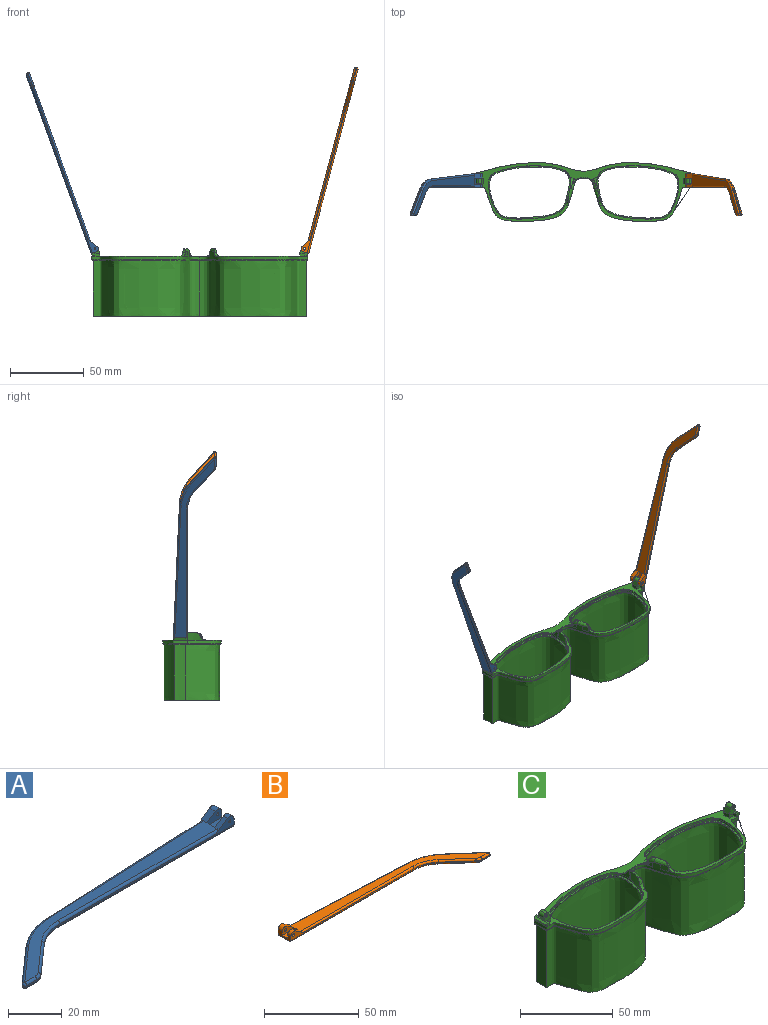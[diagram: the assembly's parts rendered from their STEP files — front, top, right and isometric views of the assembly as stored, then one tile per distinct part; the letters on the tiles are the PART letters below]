
ASSEMBLY  parts=3 mates=2
PART A: 43 faces, bbox 130.2x29.5x5.9 mm
  f0: plane 9.62x3.72mm, normal (1,0,0), area 24.7mm2, adj f1,f3,f4,f5,f10,f16,f18,f28
  f1: cylinder r=2.2mm len=3.45mm, axis (0,-1,0), area 11mm2, adj f0,f2,f4,f37
  f2: plane 6.01x3.91mm, normal (-0.55,0,0.84), area 12.7mm2, adj f1,f4,f9,f19,f37
  f3: plane 2.26x0.1mm, normal (0,0,1), area 0.1mm2, adj f0,f5,f18
  f4: plane 92.1x4.9mm, normal (0,-1,0), area 79.9mm2, adj f0,f1,f2,f14,f19,f36,f42
  f5: plane 93.42x4.13mm, normal (-0.04,1,0), area 64.8mm2, adj f0,f3,f11,f15,f17,f27,f28
  f6: plane 17.82x15.72mm, normal (-0.66,0.75,0), area 14.3mm2, adj f11,f12,f25,f30
  f7: plane 5.46x0.6mm, normal (0,-1,0), area 3.3mm2, adj f12,f13,f23,f32
  f8: plane 14.99x13.23mm, normal (0.66,-0.75,0), area 12mm2, adj f13,f14,f21,f34
  f9: plane 121.18x26.73mm, normal (0,0,1), area 627.7mm2, adj f2,f17,f19,f20,f21,f22,f23,f25
  f10: plane 129.1x27.08mm, normal (0,0,-1), area 686.5mm2, adj f0,f28,f29,f30,f32,f33,f34,f35
  f11: cylinder r=30mm len=18.52mm, axis (0,0,-1), area 12.2mm2, adj f5,f6,f26,f29
  f12: cylinder r=1mm len=1.75mm, axis (0,0,-1), area 1.5mm2, adj f6,f7,f24,f31
  f13: cylinder r=5mm len=3.31mm, axis (0,0,-1), area 2.2mm2, adj f7,f8,f22,f33
  f14: cylinder r=20mm len=13.23mm, axis (0,0,1), area 8.7mm2, adj f4,f8,f20,f35
  f15: plane 5.66x0.25mm, normal (0,0,-1), area 0.7mm2, adj f5,f17,f18
  f16: cylinder r=2.2mm len=3.45mm, axis (0,-1,0), area 14.8mm2, adj f0,f17,f18,f38
  f17: plane 6.01x3.91mm, normal (-0.55,0,0.84), area 16.9mm2, adj f5,f9,f15,f16,f18,f27,f38
  f18: plane 7.92x3.3mm, normal (0,1,0), area 15.9mm2, adj f0,f3,f15,f16,f17,f41
  f19: cylinder r=1mm len=84.18mm, axis (-1,0,0), area 131.4mm2, adj f2,f4,f9,f20
  f20: torus R=21mm, axis (0,0,1), area 23.1mm2, adj f9,f14,f19,f21
  f21: cylinder r=1mm len=15.65mm, axis (-0.75,-0.66,0), area 31.4mm2, adj f8,f9,f20,f22
  f22: torus R=4mm, axis (0,0,1), area 5.3mm2, adj f9,f13,f21,f23
  f23: cylinder r=1mm len=5.46mm, axis (-1,0,0), area 8.6mm2, adj f7,f9,f22,f24
  f24: sphere r=1mm, area 2.4mm2, adj f12,f23,f25
  f25: cylinder r=1mm len=18.48mm, axis (0.75,0.66,0), area 37.3mm2, adj f6,f9,f24,f26
  f26: torus R=29mm, axis (0,0,1), area 31.6mm2, adj f9,f11,f25,f27
  f27: cylinder r=1mm len=85.5mm, axis (1,0.04,0), area 133.5mm2, adj f5,f9,f17,f26
  f28: cylinder r=1mm len=93.46mm, axis (-1,-0.04,0), area 146.9mm2, adj f0,f5,f10,f29
  f29: torus R=29mm, axis (0,0,1), area 31.6mm2, adj f10,f11,f28,f30
  f30: cylinder r=1mm len=18.48mm, axis (-0.75,-0.66,0), area 37.3mm2, adj f6,f10,f29,f31
  f31: sphere r=1mm, area 2.4mm2, adj f12,f30,f32
  f32: cylinder r=1mm len=5.46mm, axis (1,0,0), area 8.6mm2, adj f7,f10,f31,f33
  f33: torus R=4mm, axis (0,0,1), area 5.3mm2, adj f10,f13,f32,f34
  f34: cylinder r=1mm len=15.65mm, axis (0.75,0.66,0), area 31.4mm2, adj f8,f10,f33,f35
  f35: torus R=21mm, axis (0,0,1), area 23.1mm2, adj f10,f14,f34,f36
  f36: cylinder r=1mm len=92.1mm, axis (1,0,0), area 144.7mm2, adj f0,f4,f10,f35
  f37: plane 7.92x4.7mm, normal (0,1,0), area 27mm2, adj f0,f1,f2,f39,f40,f42
  f38: plane 7.92x4.7mm, normal (0,-1,0), area 27mm2, adj f0,f16,f17,f39,f40,f41
  f39: plane 7.92x4.1mm, normal (0,0,1), area 32.5mm2, adj f0,f37,f38,f40
  f40: plane 4.1x1.4mm, normal (1,0,0), area 5.7mm2, adj f9,f37,f38,f39
  f41: cylinder r=0.5mm len=3.1mm, axis (0,-1,0), area 9.7mm2, adj f18,f38
  f42: cylinder r=0.5mm len=2.3mm, axis (0,-1,0), area 7.2mm2, adj f4,f37
PART B: 43 faces, bbox 130.2x29.5x5.9 mm
  f0: plane 9.62x3.72mm, normal (-1,0,0), area 24.7mm2, adj f1,f3,f4,f5,f10,f16,f18,f28
  f1: cylinder r=2.2mm len=3.45mm, axis (0,-1,0), area 11mm2, adj f0,f2,f4,f37
  f2: plane 6.01x3.91mm, normal (0.55,0,0.84), area 12.7mm2, adj f1,f4,f9,f19,f37
  f3: plane 2.26x0.1mm, normal (0,0,1), area 0.1mm2, adj f0,f5,f18
  f4: plane 92.1x4.9mm, normal (0,-1,0), area 78.2mm2, adj f0,f1,f2,f14,f19,f36,f42
  f5: plane 93.42x4.13mm, normal (0.04,1,0), area 64.8mm2, adj f0,f3,f11,f15,f17,f27,f28
  f6: plane 17.82x15.72mm, normal (0.66,0.75,0), area 14.3mm2, adj f11,f12,f25,f30
  f7: plane 5.46x0.6mm, normal (0,-1,0), area 3.3mm2, adj f12,f13,f23,f32
  f8: plane 14.99x13.23mm, normal (-0.66,-0.75,0), area 12mm2, adj f13,f14,f21,f34
  f9: plane 121.18x26.73mm, normal (0,0,1), area 627.7mm2, adj f2,f17,f19,f20,f21,f22,f23,f25
  f10: plane 129.1x27.08mm, normal (0,0,-1), area 686.5mm2, adj f0,f28,f29,f30,f32,f33,f34,f35
  f11: cylinder r=30mm len=18.52mm, axis (0,0,-1), area 12.2mm2, adj f5,f6,f26,f29
  f12: cylinder r=1mm len=1.75mm, axis (0,0,-1), area 1.5mm2, adj f6,f7,f24,f31
  f13: cylinder r=5mm len=3.31mm, axis (0,0,-1), area 2.2mm2, adj f7,f8,f22,f33
  f14: cylinder r=20mm len=13.23mm, axis (0,0,1), area 8.7mm2, adj f4,f8,f20,f35
  f15: plane 5.66x0.25mm, normal (0,0,-1), area 0.7mm2, adj f5,f17,f18
  f16: cylinder r=2.2mm len=3.45mm, axis (0,-1,0), area 14.8mm2, adj f0,f17,f18,f38
  f17: plane 6.01x3.91mm, normal (0.55,0,0.84), area 16.9mm2, adj f5,f9,f15,f16,f18,f27,f38
  f18: plane 7.92x3.3mm, normal (0,1,0), area 14.3mm2, adj f0,f3,f15,f16,f17,f41
  f19: cylinder r=1mm len=84.18mm, axis (1,0,0), area 131.4mm2, adj f2,f4,f9,f20
  f20: torus R=21mm, axis (0,0,1), area 23.1mm2, adj f9,f14,f19,f21
  f21: cylinder r=1mm len=15.65mm, axis (0.75,-0.66,0), area 31.4mm2, adj f8,f9,f20,f22
  f22: torus R=4mm, axis (0,0,1), area 5.3mm2, adj f9,f13,f21,f23
  f23: cylinder r=1mm len=5.46mm, axis (1,0,0), area 8.6mm2, adj f7,f9,f22,f24
  f24: sphere r=1mm, area 2.4mm2, adj f12,f23,f25
  f25: cylinder r=1mm len=18.48mm, axis (-0.75,0.66,0), area 37.3mm2, adj f6,f9,f24,f26
  f26: torus R=29mm, axis (0,0,1), area 31.6mm2, adj f9,f11,f25,f27
  f27: cylinder r=1mm len=85.5mm, axis (-1,0.04,0), area 133.5mm2, adj f5,f9,f17,f26
  f28: cylinder r=1mm len=93.46mm, axis (1,-0.04,0), area 146.9mm2, adj f0,f5,f10,f29
  f29: torus R=29mm, axis (0,0,1), area 31.6mm2, adj f10,f11,f28,f30
  f30: cylinder r=1mm len=18.48mm, axis (0.75,-0.66,0), area 37.3mm2, adj f6,f10,f29,f31
  f31: sphere r=1mm, area 2.4mm2, adj f12,f30,f32
  f32: cylinder r=1mm len=5.46mm, axis (-1,0,0), area 8.6mm2, adj f7,f10,f31,f33
  f33: torus R=4mm, axis (0,0,1), area 5.3mm2, adj f10,f13,f32,f34
  f34: cylinder r=1mm len=15.65mm, axis (-0.75,0.66,0), area 31.4mm2, adj f8,f10,f33,f35
  f35: torus R=21mm, axis (0,0,1), area 23.1mm2, adj f10,f14,f34,f36
  f36: cylinder r=1mm len=92.1mm, axis (-1,0,0), area 144.7mm2, adj f0,f4,f10,f35
  f37: plane 7.92x4.7mm, normal (0,1,0), area 25.4mm2, adj f0,f1,f2,f39,f40,f42
  f38: plane 7.92x4.7mm, normal (0,-1,0), area 25.4mm2, adj f0,f16,f17,f39,f40,f41
  f39: plane 7.92x4.1mm, normal (0,0,1), area 32.5mm2, adj f0,f37,f38,f40
  f40: plane 4.1x1.4mm, normal (-1,0,0), area 5.7mm2, adj f9,f37,f38,f39
  f41: cylinder r=0.88mm len=3.1mm, axis (0,-1,0), area 17mm2, adj f18,f38
  f42: cylinder r=0.88mm len=2.3mm, axis (0,-1,0), area 12.6mm2, adj f4,f37
PART C: 128 faces, bbox 148.1x40.9x48.5 mm
  f0: bspline ~1.82x1.22mm, area 0.7mm2, adj f2,f7,f36,f51
  f1: plane 147.73x40.5mm, normal (0,0,1), area 772.9mm2, adj f4,f5,f6,f7,f8,f11,f19,f22
  f2: bspline ~5.39x4.93mm, area 12.7mm2, adj f0,f7,f36,f40,f42,f51,f52
  f3: plane 4.46x1.45mm, normal (0,0,1), area 0.1mm2, adj f7,f37
  f4: plane 1.23x0.04mm, normal (0,0,1), area 0mm2, adj f1,f7,f21
  f5: plane 6.97x5.07mm, normal (0,1,0), area 22.7mm2, adj f1,f19,f20,f24,f26,f27,f29,f30
  f6: plane 3.2x2.36mm, normal (0,-1,0), area 5.7mm2, adj f1,f19,f25,f28
  f7: extruded ~73.26x39.84mm, area 292.7mm2, adj f0,f1,f2,f3,f4,f8,f12,f13
  f8: extruded ~35.39x5.69mm, area 72.2mm2, adj f1,f7,f17,f66
  f9: plane 56.03x36.25mm, normal (0,0,1), area 125.7mm2, adj f10,f18
  f10: extruded ~55.63x36.1mm, area 160.7mm2, adj f9,f11
  f11: extruded ~55.63x36.1mm, area 220.4mm2, adj f1,f10,f38,f39,f40,f41,f42,f43
  f12: bspline ~73.27x30.39mm, area 161.7mm2, adj f7,f13,f70,f117
  f13: bspline ~1x1mm, area 0.8mm2, adj f7,f12,f14
  f14: bspline ~8.32x1.19mm, area 12.6mm2, adj f7,f13,f15,f124
  f15: bspline ~1.04x1mm, area 0.7mm2, adj f7,f14,f16
  f16: bspline ~45.86x8.59mm, area 59.8mm2, adj f7,f15,f17,f123
  f17: bspline ~37.01x6.7mm, area 56.6mm2, adj f8,f16,f75,f122
  f18: bspline ~56.1x36.66mm, area 237.6mm2, adj f9,f125
  f19: plane 4x2.36mm, normal (-1,0,0), area 9.5mm2, adj f1,f5,f6,f20
  f20: plane 4x0.02mm, normal (0.34,0,0.94), area 0.1mm2, adj f5,f19,f27
  f21: plane 2.76x2.53mm, normal (0,-1,0), area 3.9mm2, adj f4,f25,f26,f34,f55
  f22: plane 7.67x1.6mm, normal (0.94,0,-0.34), area 13mm2, adj f1,f34,f35,f55
  f23: plane 2.1x1.69mm, normal (0,1,0), area 2.8mm2, adj f1,f24,f26,f35,f55
  f24: plane 3.3x2.1mm, normal (-1,0,0), area 6.9mm2, adj f1,f5,f23,f26
  f25: plane 2.35x2.1mm, normal (-1,0,0), area 4.9mm2, adj f1,f6,f21,f26,f28
  f26: plane 9.65x1.24mm, normal (0,0,1), area 8.2mm2, adj f5,f21,f23,f24,f25,f28,f29,f55
  f27: plane 4x3.31mm, normal (-0.94,0,0.34), area 14.1mm2, adj f5,f20,f28,f31
  f28: plane 5.77x5.06mm, normal (0,-1,0), area 17mm2, adj f6,f25,f26,f27,f29,f30,f31,f32
  f29: plane 4x2.21mm, normal (0.94,0,-0.34), area 9.4mm2, adj f5,f26,f28,f32
  f30: plane 4x0.01mm, normal (0.34,0,0.94), area 0mm2, adj f5,f28,f31,f32
  f31: cylinder r=1.98mm len=4mm, axis (0,1,0), area 12.4mm2, adj f5,f27,f28,f30
  f32: cylinder r=1.98mm len=4mm, axis (0,-1,0), area 12.4mm2, adj f5,f28,f29,f30
  f33: cylinder r=0.88mm len=4mm, axis (0,-1,0), area 22mm2, adj f5,f28
  f34: cone r=1mm half-angle=20deg, axis (0,0,1), area 2.3mm2, adj f1,f21,f22,f55
  f35: cylinder r=1mm len=2.28mm, axis (-0.34,0,-0.94), area 3mm2, adj f1,f22,f23,f55
  f36: extruded ~3.67x3.11mm, area 5.9mm2, adj f0,f2,f7,f58
  f37: extruded ~4.44x3.32mm, area 15.1mm2, adj f3,f7,f41,f42,f54
  f38: extruded ~4.98x1.36mm, area 6.6mm2, adj f11,f40
  f39: plane 3.63x0.97mm, normal (0,0,1), area 0.3mm2, adj f11,f40,f42
  f40: bspline ~15.5x15.35mm, area 6.4mm2, adj f2,f11,f38,f39,f53
  f41: bspline ~7.26x7.26mm, area 6.3mm2, adj f11,f37,f42,f54
  f42: bspline ~10.29x4.84mm, area 21.4mm2, adj f2,f7,f11,f37,f39,f41
  f43: plane 2.88x1.51mm, normal (0,0,-1), area 1.8mm2, adj f11,f44
  f44: cylinder r=2.28mm len=2.86mm, axis (0,0,1), area 1.8mm2, adj f1,f11,f43,f53
  f45: plane 2.5x1.83mm, normal (0,0,-1), area 1.7mm2, adj f11,f46
  f46: cylinder r=2.28mm len=2.47mm, axis (0,0,1), area 1.7mm2, adj f1,f11,f45
  f47: plane 1.79x1.31mm, normal (0,0,-1), area 0.9mm2, adj f11,f48
  f48: cylinder r=1.3mm len=1.78mm, axis (0,0,1), area 1.3mm2, adj f1,f11,f47
  f49: plane 1.95x1.68mm, normal (0,0,-1), area 1.5mm2, adj f11,f50
  f50: cylinder r=1.3mm len=1.93mm, axis (0,0,1), area 1.5mm2, adj f1,f11,f49
  f51: bspline ~2.66x2.04mm, area 1.9mm2, adj f0,f2,f7,f52,f57
  f52: bspline ~3.55x3.47mm, area 3.7mm2, adj f1,f2,f51,f53,f57
  f53: bspline ~5.1x3.97mm, area 7.6mm2, adj f1,f11,f40,f44,f52
  f54: bspline ~3.7x3.66mm, area 7.8mm2, adj f1,f7,f11,f37,f41
  f55: plane 9.71x1.44mm, normal (0.34,0,0.94), area 13.9mm2, adj f21,f22,f23,f26,f34,f35
  f56: bspline ~6.38x2.14mm, area 2.6mm2, adj f1,f7,f57,f114
  f57: bspline ~2.1x1.46mm, area 0.6mm2, adj f7,f51,f52,f56
  f58: bspline ~5.24x1.75mm, area 0mm2, adj f7,f36
  f59: bspline ~2.19x1.4mm, area 0.7mm2, adj f60,f65,f94,f109
  f60: bspline ~6.1x4.93mm, area 12.6mm2, adj f59,f65,f94,f98,f100,f109,f110
  f61: plane 4.46x1.45mm, normal (0,0,1), area 0.1mm2, adj f65,f95
  f62: plane 1.23x0.04mm, normal (0,0,1), area 0mm2, adj f1,f65,f79
  f63: plane 6.97x5.07mm, normal (0,1,0), area 22.7mm2, adj f1,f77,f78,f82,f84,f85,f87,f88
  f64: plane 3.2x2.36mm, normal (0,-1,0), area 5.7mm2, adj f1,f77,f83,f86
  f65: extruded ~73.26x39.84mm, area 292.7mm2, adj f1,f7,f59,f60,f61,f62,f66,f70
  f66: extruded ~35.39x5.69mm, area 72.2mm2, adj f1,f8,f65,f75
  f67: plane 56.31x36.53mm, normal (0,0,1), area 124.8mm2, adj f68,f76
  f68: extruded ~55.63x36.1mm, area 160.7mm2, adj f67,f69
  f69: extruded ~55.63x36.1mm, area 220.4mm2, adj f1,f68,f96,f97,f98,f99,f100,f101
  f70: bspline ~73.83x30.39mm, area 161.7mm2, adj f12,f65,f71,f118
  f71: bspline ~1x1mm, area 0.8mm2, adj f65,f70,f72
  f72: bspline ~8.99x1.23mm, area 12.6mm2, adj f65,f71,f73,f119
  f73: bspline ~1.04x1mm, area 0.8mm2, adj f65,f72,f74
  f74: bspline ~37.64x7.99mm, area 59.8mm2, adj f65,f73,f75,f120
  f75: bspline ~37.01x6.7mm, area 56.6mm2, adj f17,f66,f74,f121
  f76: bspline ~56.07x36.64mm, area 237.6mm2, adj f67,f126
  f77: plane 4x2.36mm, normal (1,0,0), area 9.5mm2, adj f1,f63,f64,f78
  f78: plane 4x0.02mm, normal (-0.34,0,0.94), area 0.1mm2, adj f63,f77,f85
  f79: plane 2.76x2.53mm, normal (0,-1,0), area 3.9mm2, adj f62,f83,f84,f92,f113
  f80: plane 7.67x1.6mm, normal (-0.94,0,-0.34), area 13mm2, adj f1,f92,f93,f113
  f81: plane 2.1x1.69mm, normal (0,1,0), area 2.8mm2, adj f1,f82,f84,f93,f113
  f82: plane 3.3x2.1mm, normal (1,0,0), area 6.9mm2, adj f1,f63,f81,f84
  f83: plane 2.35x2.1mm, normal (1,0,0), area 4.9mm2, adj f1,f64,f79,f84,f86
  f84: plane 9.65x1.24mm, normal (0,0,1), area 8.2mm2, adj f63,f79,f81,f82,f83,f86,f87,f113
  f85: plane 4x3.31mm, normal (0.94,0,0.34), area 14.1mm2, adj f63,f78,f86,f89
  f86: plane 5.77x5.06mm, normal (0,-1,0), area 17mm2, adj f64,f83,f84,f85,f87,f88,f89,f90
  f87: plane 4x2.21mm, normal (-0.94,0,-0.34), area 9.4mm2, adj f63,f84,f86,f90
  f88: plane 4x0.01mm, normal (-0.34,0,0.94), area 0mm2, adj f63,f86,f89,f90
  f89: cylinder r=1.98mm len=4mm, axis (0,1,0), area 12.4mm2, adj f63,f85,f86,f88
  f90: cylinder r=1.98mm len=4mm, axis (0,-1,0), area 12.4mm2, adj f63,f86,f87,f88
  f91: cylinder r=0.88mm len=4mm, axis (0,-1,0), area 22mm2, adj f63,f86
  f92: cone r=1mm half-angle=20deg, axis (0,0,1), area 2.3mm2, adj f1,f79,f80,f113
  f93: cylinder r=1mm len=2.28mm, axis (0.34,0,-0.94), area 3mm2, adj f1,f80,f81,f113
  f94: extruded ~3.67x3.11mm, area 5.9mm2, adj f59,f60,f65,f116
  f95: extruded ~4.44x3.32mm, area 15.1mm2, adj f61,f65,f99,f100,f112
  f96: extruded ~4.98x1.36mm, area 6.6mm2, adj f69,f98
  f97: plane 3.63x0.97mm, normal (0,0,1), area 0.3mm2, adj f69,f98,f100
  f98: bspline ~15.5x15.35mm, area 6.4mm2, adj f60,f69,f96,f97,f111
  f99: bspline ~7.26x7.26mm, area 6.2mm2, adj f69,f95,f100,f112
  f100: bspline ~10.29x4.84mm, area 21.5mm2, adj f60,f65,f69,f95,f97,f99
  f101: plane 2.88x1.51mm, normal (0,0,-1), area 1.8mm2, adj f69,f102
  f102: cylinder r=2.28mm len=2.86mm, axis (0,0,1), area 1.8mm2, adj f1,f69,f101,f111
  f103: plane 2.5x1.83mm, normal (0,0,-1), area 1.7mm2, adj f69,f104
  f104: cylinder r=2.28mm len=2.47mm, axis (0,0,1), area 1.7mm2, adj f1,f69,f103
  f105: plane 1.79x1.31mm, normal (0,0,-1), area 0.9mm2, adj f69,f106
  f106: cylinder r=1.3mm len=1.78mm, axis (0,0,1), area 1.3mm2, adj f1,f69,f105
  f107: plane 1.95x1.68mm, normal (0,0,-1), area 1.5mm2, adj f69,f108
  f108: cylinder r=1.3mm len=1.93mm, axis (0,0,1), area 1.5mm2, adj f1,f69,f107
  f109: bspline ~2.65x2.03mm, area 1.9mm2, adj f59,f60,f65,f110,f115
  f110: bspline ~3.55x3.47mm, area 3.7mm2, adj f1,f60,f109,f111,f115
  f111: bspline ~4.88x3.94mm, area 7.6mm2, adj f1,f69,f98,f102,f110
  f112: bspline ~3.7x3.66mm, area 7.8mm2, adj f1,f65,f69,f95,f99
  f113: plane 9.71x1.44mm, normal (-0.34,0,0.94), area 13.9mm2, adj f79,f80,f81,f84,f92,f93
  f114: bspline ~6.38x2.14mm, area 2.6mm2, adj f1,f56,f65,f115
  f115: bspline ~2.1x1.46mm, area 0.6mm2, adj f65,f109,f110,f114
  f116: bspline ~5.24x1.75mm, area 0mm2, adj f65,f94
  f117: extruded ~72.24x38mm, area 3904.3mm2, adj f12,f118,f124,f127
  f118: extruded ~72.24x38mm, area 3904.3mm2, adj f70,f117,f119,f127
  f119: extruded ~38x7.91mm, area 300.8mm2, adj f72,f118,f120,f127
  f120: extruded ~38x37.03mm, area 1435.4mm2, adj f74,f119,f121,f127
  f121: extruded ~38x35.36mm, area 1369.7mm2, adj f75,f120,f122,f127
  f122: extruded ~38x35.36mm, area 1369.7mm2, adj f17,f121,f123,f127
  f123: extruded ~38x37.03mm, area 1435.4mm2, adj f16,f122,f124,f127
  f124: extruded ~38x7.91mm, area 300.8mm2, adj f14,f117,f123,f127
  f125: extruded ~56.13x38mm, area 5898.3mm2, adj f18,f127
  f126: extruded ~56.13x38mm, area 5898.3mm2, adj f76,f127
  f127: plane 145.27x38.34mm, normal (0,0,-1), area 524.4mm2, adj f117,f118,f119,f120,f121,f122,f123,f124
PLACE A rot(axis=(0,1,0),70deg) t=(-84.77,-5.75,56)mm
PLACE B rot(axis=(0,-1,0),75deg) t=(68.2,-5.75,-61.61)mm
PLACE C t=(10.15,-1.13,-5.77)mm
MATE revolute A.f1 <-> C.f89  axis (0,-1,0) through (-60.89,2.72,1.22)mm
MATE revolute B.f41 <-> C.f32  axis (0,-1,0) through (81.2,2.72,1.21)mm
